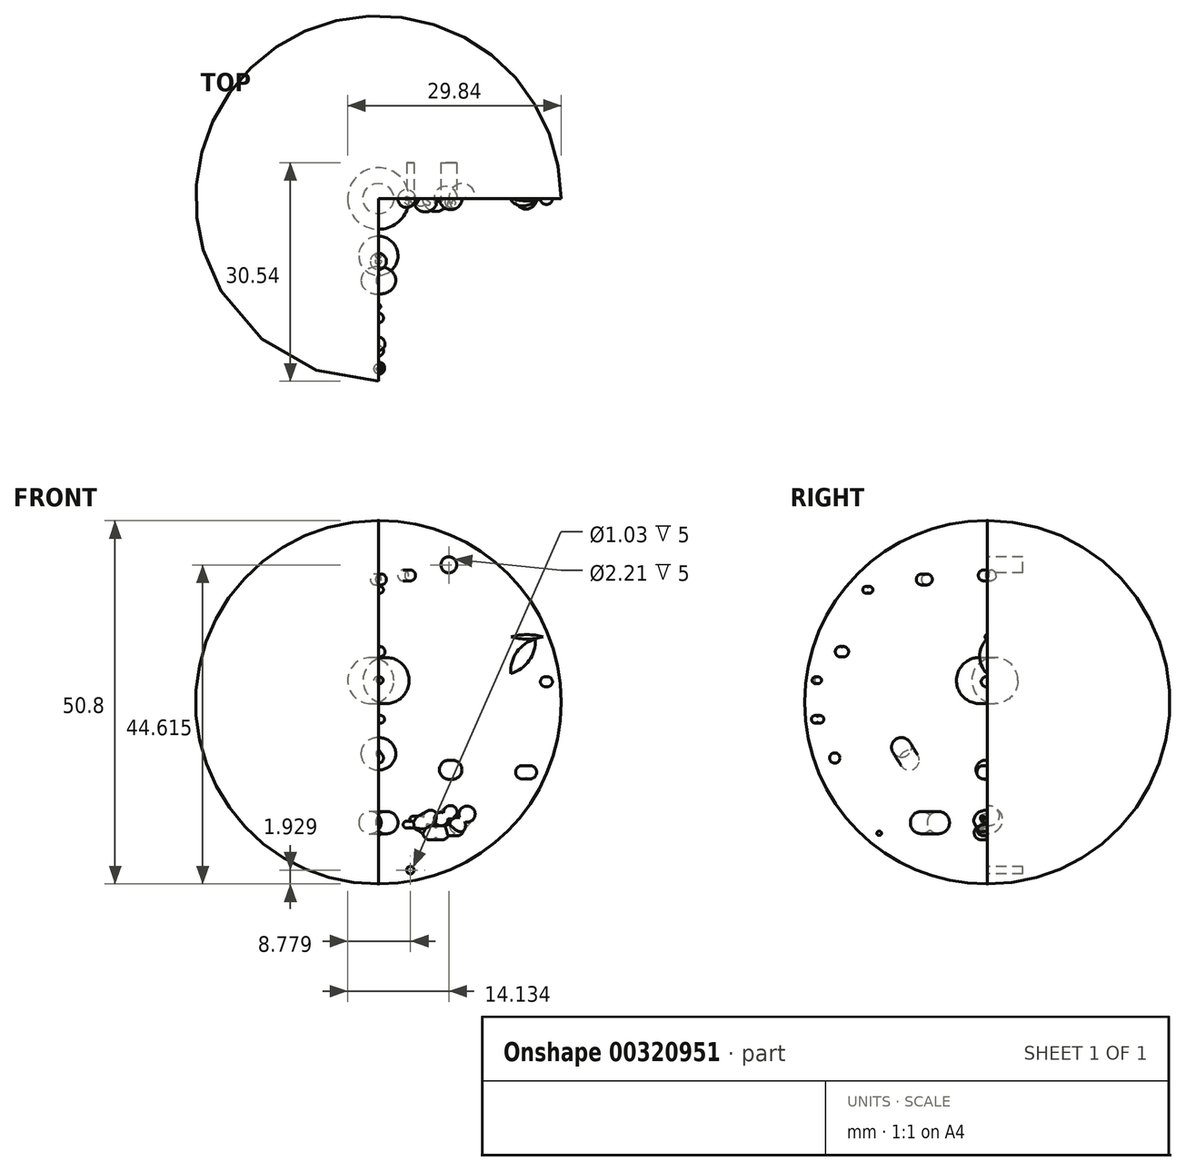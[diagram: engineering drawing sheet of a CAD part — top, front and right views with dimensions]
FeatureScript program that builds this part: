
annotation { "Feature Type Name" : "Feature", "Feature Type Description" : "" }
export const myFeature = defineFeature(function(context is Context, id is Id, definition is map)
    precondition{}
    {
        {
            var Q0;
            Q0=qCreatedBy(makeId("Front.planeOp"),FACE);
            var sketch = newSketch(context, id + "F0", { "sketchPlane" : qUnion([Q0])});
            skLineSegment(sketch, "E0", {"start": v(0, 0) * mm, "end": v(0, 50.8) * mm});
            skArc(sketch, "E1", {"start": v(0, 0) * mm, "mid": v(25.54, 25.4) * mm, "end": v(0, 50.8) * mm});
            skSolve(sketch);
        }
        {
            var Q0;
            Q0=makeQuery(id+"F0.imprint","IMPRINT",FACE,{"disambiguationData":[TD([[makeQuery(id+"F0.imprint","IMPRINT",EDGE,{"derivedFrom":sQuery(id+"F0.wireOp",EDGE,"E0")}),-1.0]])]});
            var Q1;
            Q1=sQuery(id+"F0.wireOp",EDGE,"E0");
            revolve(context, id + "F1", {"entities" : qUnion([Q0]), "axis" : qUnion([Q1]), "revolveType" : RevolveType.ONE_DIRECTION, "angle" : 270 * degree});
        }
        {
            var Q0;
            Q0=makeQuery(id+"F1.opRevolve","CAP_FACE",FACE,{"disambiguationData":[OSD([sQuery(id+"F0.wireOp",EDGE,"E0"),sQuery(id+"F0.wireOp",EDGE,"E1")])],"isStart":false});
            var sketch = newSketch(context, id + "F2", { "sketchPlane" : qUnion([Q0])});
            skLineSegment(sketch, "E2", {"start": v(0, 25.4) * mm, "end": v(0, 31.48) * mm});
            skArc(sketch, "E3", {"start": v(0, 31.48) * mm, "mid": v(-4.3, 28.44) * mm, "end": v(0, 25.4) * mm});
            skSolve(sketch);
        }
        {
            var Q0;
            Q0=makeQuery(id+"F2.imprint","IMPRINT",FACE,{"disambiguationData":[TD([[makeQuery(id+"F2.imprint","IMPRINT",EDGE,{"derivedFrom":sQuery(id+"F2.wireOp",EDGE,"E2")}),1.0]])]});
            var Q1;
            Q1=sQuery(id+"F2.wireOp",EDGE,"E2");
            revolve(context, id + "F3", {"entities" : qUnion([Q0]), "axis" : qUnion([Q1]), "revolveType" : RevolveType.FULL});
        }
        {
            var Q0;
            Q0=makeQuery(id+"F0.imprint","IMPRINT",FACE,{"disambiguationData":[TD([[makeQuery(id+"F0.imprint","IMPRINT",EDGE,{"derivedFrom":sQuery(id+"F0.wireOp",EDGE,"E0")}),-1.0]])]});
            var sketch = newSketch(context, id + "F4", { "sketchPlane" : qUnion([Q0])});
            skLineSegment(sketch, "E4", {"start": v(14.97, 35.22) * mm, "end": v(14.97, 32.76) * mm});
            skArc(sketch, "E5", {"start": v(14.97, 35.22) * mm, "mid": v(13.5, 33.99) * mm, "end": v(14.97, 32.76) * mm});
            skSolve(sketch);
        }
        {
            var Q0;
            Q0=sQuery(id+"F4.wireOp",EDGE,"E5");
            var Q1;
            Q1=sQuery(id+"F4.wireOp",EDGE,"E4");
            revolve(context, id + "F5", {"bodyType" : ToolBodyType.SURFACE, "surfaceEntities" : qUnion([Q0]), "axis" : qUnion([Q1]), "revolveType" : RevolveType.FULL});
        }
        {
            var Q0;
            Q0=makeQuery(id+"F0.imprint","IMPRINT",FACE,{"disambiguationData":[TD([[makeQuery(id+"F0.imprint","IMPRINT",EDGE,{"derivedFrom":sQuery(id+"F0.wireOp",EDGE,"E0")}),-1.0]])]});
            var sketch = newSketch(context, id + "F6", { "sketchPlane" : qUnion([Q0])});
            skLineSegment(sketch, "E6", {"start": v(10.1, 14.64) * mm, "end": v(10.1, 17.28) * mm});
            skArc(sketch, "E7", {"start": v(10.1, 14.64) * mm, "mid": v(11.67, 15.96) * mm, "end": v(10.1, 17.28) * mm});
            skSolve(sketch);
        }
        {
            var Q0;
            Q0=makeQuery(id+"F6.imprint","IMPRINT",FACE,{"disambiguationData":[TD([[makeQuery(id+"F6.imprint","IMPRINT",EDGE,{"derivedFrom":sQuery(id+"F6.wireOp",EDGE,"E6")}),-1.0]])]});
            var Q1;
            Q1=sQuery(id+"F6.wireOp",EDGE,"E6");
            revolve(context, id + "F7", {"operationType" : NewBodyOperationType.ADD, "entities" : qUnion([Q0]), "axis" : qUnion([Q1]), "revolveType" : RevolveType.FULL});
        }
        {
            var Q0;
            {var subQ0=sQuery(id+"F2.wireOp",EDGE,"E3");Q0=makeQuery(id+"F2.imprint","IMPRINT",FACE,{"disambiguationData":[TD([[makeQuery(id+"F2.imprint","IMPRINT",EDGE,{"derivedFrom":subQ0}),-1.0]])]});}
            var sketch = newSketch(context, id + "F8", { "sketchPlane" : qUnion([Q0])});
            skLineSegment(sketch, "E8", {"start": v(-21.3, 16.88) * mm, "end": v(-21.3, 18.33) * mm});
            skArc(sketch, "E9", {"start": v(-21.3, 16.88) * mm, "mid": v(-20.58, 17.6) * mm, "end": v(-21.3, 18.33) * mm});
            skSolve(sketch);
        }
        {
            var Q0;
            Q0=makeQuery(id+"F8.imprint","IMPRINT",FACE,{"disambiguationData":[TD([[makeQuery(id+"F8.imprint","IMPRINT",EDGE,{"derivedFrom":sQuery(id+"F8.wireOp",EDGE,"E8")}),-1.0]])]});
            var Q1;
            Q1=sQuery(id+"F8.wireOp",EDGE,"E8");
            revolve(context, id + "F9", {"operationType" : NewBodyOperationType.ADD, "entities" : qUnion([Q0]), "axis" : qUnion([Q1]), "revolveType" : RevolveType.FULL});
        }
        {
            var Q0;
            {var subQ0=sQuery(id+"F2.wireOp",EDGE,"E3");Q0=makeQuery(id+"F2.imprint","IMPRINT",FACE,{"disambiguationData":[TD([[makeQuery(id+"F2.imprint","IMPRINT",EDGE,{"derivedFrom":subQ0}),-1.0]])]});}
            var sketch = newSketch(context, id + "F10", { "sketchPlane" : qUnion([Q0])});
            skLineSegment(sketch, "E10", {"start": v(-16.7, 40.71) * mm, "end": v(-16.7, 41.53) * mm});
            skArc(sketch, "E11", {"start": v(-16.7, 40.71) * mm, "mid": v(-16, 41.12) * mm, "end": v(-16.7, 41.53) * mm});
            skSolve(sketch);
        }
        {
            var Q0;
            Q0 = qSketchRegion(id + "F10", true);
            var Q1;
            Q1=sQuery(id+"F10.wireOp",EDGE,"E10");
            revolve(context, id + "F11", {"operationType" : NewBodyOperationType.ADD, "entities" : qUnion([Q0]), "axis" : qUnion([Q1]), "revolveType" : RevolveType.FULL});
        }
        {
            var Q0;
            {var subQ0=sQuery(id+"F2.wireOp",EDGE,"E3");Q0=makeQuery(id+"F2.imprint","IMPRINT",FACE,{"disambiguationData":[TD([[makeQuery(id+"F2.imprint","IMPRINT",EDGE,{"derivedFrom":subQ0}),-1.0]])]});}
            var sketch = newSketch(context, id + "F12", { "sketchPlane" : qUnion([Q0])});
            skLineSegment(sketch, "E12", {"start": v(-15.1, 6.78) * mm, "end": v(-15.1, 7.37) * mm});
            skArc(sketch, "E13", {"start": v(-15.1, 6.78) * mm, "mid": v(-14.78, 7.08) * mm, "end": v(-15.1, 7.37) * mm});
            skSolve(sketch);
        }
        {
            var Q0;
            Q0 = qSketchRegion(id + "F12", true);
            var Q1;
            Q1=sQuery(id+"F12.wireOp",EDGE,"E12");
            revolve(context, id + "F13", {"operationType" : NewBodyOperationType.ADD, "entities" : qUnion([Q0]), "axis" : qUnion([Q1]), "revolveType" : RevolveType.FULL});
        }
        {
            var Q0;
            {var subQ0=sQuery(id+"F2.wireOp",EDGE,"E3");Q0=makeQuery(id+"F2.imprint","IMPRINT",FACE,{"disambiguationData":[TD([[makeQuery(id+"F2.imprint","IMPRINT",EDGE,{"derivedFrom":subQ0}),-1.0]])]});}
            var sketch = newSketch(context, id + "F14", { "sketchPlane" : qUnion([Q0])});
            skLineSegment(sketch, "E14", {"start": v(-23.82, 28.05) * mm, "end": v(-23.82, 28.9) * mm});
            skArc(sketch, "E15", {"start": v(-23.82, 28.05) * mm, "mid": v(-23.16, 28.48) * mm, "end": v(-23.82, 28.9) * mm});
            skSolve(sketch);
        }
        {
            var Q0;
            Q0 = qSketchRegion(id + "F14", true);
            var Q1;
            Q1=sQuery(id+"F14.wireOp",EDGE,"E14");
            revolve(context, id + "F15", {"entities" : qUnion([Q0]), "axis" : qUnion([Q1]), "revolveType" : RevolveType.FULL});
        }
        {
            var Q0;
            {var subQ0=sQuery(id+"F2.wireOp",EDGE,"E3");Q0=makeQuery(id+"F2.imprint","IMPRINT",FACE,{"disambiguationData":[TD([[makeQuery(id+"F2.imprint","IMPRINT",EDGE,{"derivedFrom":subQ0}),-1.0]])]});}
            var sketch = newSketch(context, id + "F16", { "sketchPlane" : qUnion([Q0])});
            skLineSegment(sketch, "E16", {"start": v(-8.01, 7.55) * mm, "end": v(-8.01, 9.6) * mm});
            skArc(sketch, "E17", {"start": v(-8.01, 9.6) * mm, "mid": v(-10.75, 8.57) * mm, "end": v(-8.01, 7.55) * mm});
            skSolve(sketch);
        }
        {
            var Q0;
            Q0 = qSketchRegion(id + "F16", true);
            var Q1;
            Q1=sQuery(id+"F16.wireOp",EDGE,"E16");
            revolve(context, id + "F17", {"entities" : qUnion([Q0]), "axis" : qUnion([Q1]), "revolveType" : RevolveType.FULL});
        }
        {
            var Q0;
            {var subQ0=sQuery(id+"F2.wireOp",EDGE,"E3");Q0=makeQuery(id+"F2.imprint","IMPRINT",FACE,{"disambiguationData":[TD([[makeQuery(id+"F2.imprint","IMPRINT",EDGE,{"derivedFrom":subQ0}),-1.0]])]});}
            var sketch = newSketch(context, id + "F18", { "sketchPlane" : qUnion([Q0])});
            skLineSegment(sketch, "E18", {"start": v(-12.2, 17.73) * mm, "end": v(-10.68, 18.67) * mm});
            skArc(sketch, "E19", {"start": v(-10.68, 18.67) * mm, "mid": v(-12.72, 20.27) * mm, "end": v(-12.2, 17.73) * mm});
            skSolve(sketch);
        }
        {
            var Q0;
            Q0=makeQuery(id+"F18.imprint","IMPRINT",FACE,{"disambiguationData":[TD([[makeQuery(id+"F18.imprint","IMPRINT",EDGE,{"derivedFrom":sQuery(id+"F18.wireOp",EDGE,"E18")}),1.0]])]});
            var Q1;
            Q1=sQuery(id+"F18.wireOp",EDGE,"E18");
            revolve(context, id + "F19", {"entities" : qUnion([Q0]), "axis" : qUnion([Q1]), "revolveType" : RevolveType.FULL});
        }
        {
            var Q0;
            {var subQ0=sQuery(id+"F2.wireOp",EDGE,"E3");Q0=makeQuery(id+"F2.imprint","IMPRINT",FACE,{"disambiguationData":[TD([[makeQuery(id+"F2.imprint","IMPRINT",EDGE,{"derivedFrom":subQ0}),-1.0]])]});}
            var sketch = newSketch(context, id + "F20", { "sketchPlane" : qUnion([Q0])});
            skLineSegment(sketch, "E20", {"start": v(-8.8, 41.91) * mm, "end": v(-8.8, 43.25) * mm});
            skArc(sketch, "E21", {"start": v(-8.8, 43.25) * mm, "mid": v(-9.92, 42.58) * mm, "end": v(-8.8, 41.91) * mm});
            skSolve(sketch);
        }
        {
            var Q0;
            Q0 = qSketchRegion(id + "F20", true);
            var Q1;
            Q1=sQuery(id+"F20.wireOp",EDGE,"E20");
            revolve(context, id + "F21", {"entities" : qUnion([Q0]), "axis" : qUnion([Q1]), "revolveType" : RevolveType.FULL});
        }
        {
            var Q0;
            Q0=makeQuery(id+"F4.imprint","IMPRINT",FACE,{"disambiguationData":[TD([[makeQuery(id+"F4.imprint","IMPRINT",EDGE,{"derivedFrom":sQuery(id+"F4.wireOp",EDGE,"E4")}),1.0]])]});
            var sketch = newSketch(context, id + "F22", { "sketchPlane" : qUnion([Q0])});
            skLineSegment(sketch, "E22", {"start": v(3.95, 42.57) * mm, "end": v(3.95, 43.72) * mm});
            skArc(sketch, "E23", {"start": v(3.95, 42.57) * mm, "mid": v(5.2, 43.14) * mm, "end": v(3.95, 43.72) * mm});
            skSolve(sketch);
        }
        {
            var Q0;
            Q0 = qSketchRegion(id + "F22", true);
            var Q1;
            Q1=sQuery(id+"F22.wireOp",EDGE,"E22");
            revolve(context, id + "F23", {"entities" : qUnion([Q0]), "axis" : qUnion([Q1]), "revolveType" : RevolveType.FULL});
        }
        {
            var Q0;
            Q0=makeQuery(id+"F0.imprint","IMPRINT",FACE,{"disambiguationData":[TD([[makeQuery(id+"F0.imprint","IMPRINT",EDGE,{"derivedFrom":sQuery(id+"F0.wireOp",EDGE,"E0")}),-1.0]])]});
            var sketch = newSketch(context, id + "F24", { "sketchPlane" : qUnion([Q0])});
            skCircle(sketch, "E24", {"center": v(4.48, 1.93) * mm, "radius": 0.52 * mm});
            skSolve(sketch);
        }
        {
            var Q0;
            Q0 = qSketchRegion(id + "F24", true);
            extrude(context, id + "F25", {"entities" : qUnion([Q0]), "operationType" : NewBodyOperationType.REMOVE, "oppositeDirection" : true, "depth" : 5 * mm});
        }
        {
            var Q0;
            Q0=makeQuery(id+"F0.imprint","IMPRINT",FACE,{"disambiguationData":[TD([[makeQuery(id+"F0.imprint","IMPRINT",EDGE,{"derivedFrom":sQuery(id+"F0.wireOp",EDGE,"E0")}),-1.0]])]});
            var sketch = newSketch(context, id + "F26", { "sketchPlane" : qUnion([Q0])});
            skCircle(sketch, "E25", {"center": v(9.83, 44.62) * mm, "radius": 1.1 * mm});
            skSolve(sketch);
        }
        {
            var Q0;
            Q0 = qSketchRegion(id + "F26", true);
            extrude(context, id + "F27", {"entities" : qUnion([Q0]), "operationType" : NewBodyOperationType.REMOVE, "oppositeDirection" : true, "depth" : 5 * mm});
        }
        {
            var Q0;
            Q0=makeQuery(id+"F6.imprint","IMPRINT",FACE,{"disambiguationData":[TD([[makeQuery(id+"F6.imprint","IMPRINT",EDGE,{"derivedFrom":sQuery(id+"F6.wireOp",EDGE,"E6")}),1.0]])]});
            var sketch = newSketch(context, id + "F28", { "sketchPlane" : qUnion([Q0])});
            skLineSegment(sketch, "E26", {"start": v(4.4, 8.04) * mm, "end": v(4.4, 8.54) * mm});
            skArc(sketch, "E27", {"start": v(4.4, 8.04) * mm, "mid": v(5.33, 8.3) * mm, "end": v(4.4, 8.54) * mm});
            skSolve(sketch);
        }
        {
            var Q0;
            Q0 = qSketchRegion(id + "F28", true);
            var Q1;
            Q1=sQuery(id+"F28.wireOp",EDGE,"E26");
            revolve(context, id + "F29", {"operationType" : NewBodyOperationType.ADD, "entities" : qUnion([Q0]), "axis" : qUnion([Q1]), "revolveType" : RevolveType.FULL});
        }
        {
            var Q0;
            Q0=makeQuery(id+"F0.imprint","IMPRINT",FACE,{"disambiguationData":[TD([[makeQuery(id+"F0.imprint","IMPRINT",EDGE,{"derivedFrom":sQuery(id+"F0.wireOp",EDGE,"E0")}),-1.0]])]});
            var sketch = newSketch(context, id + "F30", { "sketchPlane" : qUnion([Q0])});
            skLineSegment(sketch, "E28", {"start": v(5.2, 8.64) * mm, "end": v(5.2, 9.33) * mm});
            skArc(sketch, "E29", {"start": v(5.2, 8.64) * mm, "mid": v(6.02, 8.99) * mm, "end": v(5.2, 9.33) * mm});
            skSolve(sketch);
        }
        {
            var Q0;
            Q0 = qSketchRegion(id + "F30", true);
            var Q1;
            Q1=sQuery(id+"F30.wireOp",EDGE,"E28");
            revolve(context, id + "F31", {"operationType" : NewBodyOperationType.ADD, "entities" : qUnion([Q0]), "axis" : qUnion([Q1]), "revolveType" : RevolveType.FULL});
        }
        {
            var Q0;
            Q0=makeQuery(id+"F4.imprint","IMPRINT",FACE,{"disambiguationData":[TD([[makeQuery(id+"F4.imprint","IMPRINT",EDGE,{"derivedFrom":sQuery(id+"F4.wireOp",EDGE,"E4")}),1.0]])]});
            var sketch = newSketch(context, id + "F32", { "sketchPlane" : qUnion([Q0])});
            skLineSegment(sketch, "E30", {"start": v(5.97, 8.18) * mm, "end": v(5.72, 7.87) * mm});
            skArc(sketch, "E31", {"start": v(5.72, 7.87) * mm, "mid": v(6.76, 7.3) * mm, "end": v(5.97, 8.18) * mm});
            skSolve(sketch);
        }
        {
            var Q0;
            Q0=makeQuery(id+"F32.imprint","IMPRINT",FACE,{"disambiguationData":[TD([[makeQuery(id+"F32.imprint","IMPRINT",EDGE,{"derivedFrom":sQuery(id+"F32.wireOp",EDGE,"E30")}),1.0]])]});
            var Q1;
            Q1=sQuery(id+"F32.wireOp",EDGE,"E30");
            revolve(context, id + "F33", {"operationType" : NewBodyOperationType.ADD, "entities" : qUnion([Q0]), "axis" : qUnion([Q1]), "revolveType" : RevolveType.FULL});
        }
        {
            var Q0;
            Q0=makeQuery(id+"F0.imprint","IMPRINT",FACE,{"disambiguationData":[TD([[makeQuery(id+"F0.imprint","IMPRINT",EDGE,{"derivedFrom":sQuery(id+"F0.wireOp",EDGE,"E0")}),-1.0]])]});
            var sketch = newSketch(context, id + "F34", { "sketchPlane" : qUnion([Q0])});
            skLineSegment(sketch, "E32", {"start": v(6.8, 8.44) * mm, "end": v(6.3, 9.3) * mm});
            skArc(sketch, "E33", {"start": v(6.8, 8.44) * mm, "mid": v(8.17, 9.8) * mm, "end": v(6.3, 9.3) * mm});
            skSolve(sketch);
        }
        {
            var Q0;
            Q0=makeQuery(id+"F34.imprint","IMPRINT",FACE,{"disambiguationData":[TD([[makeQuery(id+"F34.imprint","IMPRINT",EDGE,{"derivedFrom":sQuery(id+"F34.wireOp",EDGE,"E32")}),-1.0]])]});
            var Q1;
            Q1=sQuery(id+"F34.wireOp",EDGE,"E32");
            revolve(context, id + "F35", {"operationType" : NewBodyOperationType.ADD, "entities" : qUnion([Q0]), "axis" : qUnion([Q1]), "revolveType" : RevolveType.FULL});
        }
        {
            var Q0;
            Q0=makeQuery(id+"F0.imprint","IMPRINT",FACE,{"disambiguationData":[TD([[makeQuery(id+"F0.imprint","IMPRINT",EDGE,{"derivedFrom":sQuery(id+"F0.wireOp",EDGE,"E0")}),-1.0]])]});
            var sketch = newSketch(context, id + "F36", { "sketchPlane" : qUnion([Q0])});
            skLineSegment(sketch, "E34", {"start": v(8.03, 7.75) * mm, "end": v(8.03, 6.56) * mm});
            skArc(sketch, "E35", {"start": v(8.03, 6.56) * mm, "mid": v(9.85, 7.15) * mm, "end": v(8.03, 7.75) * mm});
            skSolve(sketch);
        }
        {
            var Q0;
            Q0 = qSketchRegion(id + "F36", true);
            var Q1;
            Q1=sQuery(id+"F36.wireOp",EDGE,"E34");
            revolve(context, id + "F37", {"operationType" : NewBodyOperationType.ADD, "entities" : qUnion([Q0]), "axis" : qUnion([Q1]), "revolveType" : RevolveType.FULL});
        }
        {
            var Q0;
            Q0=makeQuery(id+"F4.imprint","IMPRINT",FACE,{"disambiguationData":[TD([[makeQuery(id+"F4.imprint","IMPRINT",EDGE,{"derivedFrom":sQuery(id+"F4.wireOp",EDGE,"E4")}),1.0]])]});
            var sketch = newSketch(context, id + "F38", { "sketchPlane" : qUnion([Q0])});
            skLineSegment(sketch, "E36", {"start": v(9.71, 9.14) * mm, "end": v(9.12, 9.94) * mm});
            skArc(sketch, "E37", {"start": v(9.71, 9.14) * mm, "mid": v(10.83, 10.57) * mm, "end": v(9.12, 9.94) * mm});
            skSolve(sketch);
        }
        {
            var Q0;
            Q0 = qSketchRegion(id + "F38", true);
            var Q1;
            Q1=sQuery(id+"F38.wireOp",EDGE,"E36");
            revolve(context, id + "F39", {"operationType" : NewBodyOperationType.ADD, "entities" : qUnion([Q0]), "axis" : qUnion([Q1]), "revolveType" : RevolveType.FULL});
        }
        {
            var Q0;
            Q0=makeQuery(id+"F0.imprint","IMPRINT",FACE,{"disambiguationData":[TD([[makeQuery(id+"F0.imprint","IMPRINT",EDGE,{"derivedFrom":sQuery(id+"F0.wireOp",EDGE,"E0")}),-1.0]])]});
            var sketch = newSketch(context, id + "F40", { "sketchPlane" : qUnion([Q0])});
            skLineSegment(sketch, "E38", {"start": v(10.5, 7) * mm, "end": v(10.5, 8.04) * mm});
            skArc(sketch, "E39", {"start": v(10.5, 7) * mm, "mid": v(11.87, 7.52) * mm, "end": v(10.5, 8.04) * mm});
            skSolve(sketch);
        }
        {
            var Q0;
            Q0 = qSketchRegion(id + "F40", true);
            var Q1;
            Q1=sQuery(id+"F40.wireOp",EDGE,"E38");
            revolve(context, id + "F41", {"operationType" : NewBodyOperationType.ADD, "entities" : qUnion([Q0]), "axis" : qUnion([Q1]), "revolveType" : RevolveType.FULL});
        }
        {
            var Q0;
            Q0=makeQuery(id+"F4.imprint","IMPRINT",FACE,{"disambiguationData":[TD([[makeQuery(id+"F4.imprint","IMPRINT",EDGE,{"derivedFrom":sQuery(id+"F4.wireOp",EDGE,"E4")}),1.0]])]});
            var sketch = newSketch(context, id + "F42", { "sketchPlane" : qUnion([Q0])});
            skLineSegment(sketch, "E40", {"start": v(12.06, 8.69) * mm, "end": v(11.39, 9.26) * mm});
            skArc(sketch, "E41", {"start": v(12.06, 8.69) * mm, "mid": v(13.12, 10.62) * mm, "end": v(11.39, 9.26) * mm});
            skSolve(sketch);
        }
        {
            var Q0;
            Q0 = qSketchRegion(id + "F42", true);
            var Q1;
            Q1=sQuery(id+"F42.wireOp",EDGE,"E40");
            revolve(context, id + "F43", {"operationType" : NewBodyOperationType.ADD, "entities" : qUnion([Q0]), "axis" : qUnion([Q1]), "revolveType" : RevolveType.FULL});
        }
        {
            var Q0;
            Q0=makeQuery(id+"F4.imprint","IMPRINT",FACE,{"disambiguationData":[TD([[makeQuery(id+"F4.imprint","IMPRINT",EDGE,{"derivedFrom":sQuery(id+"F4.wireOp",EDGE,"E4")}),1.0]])]});
            var sketch = newSketch(context, id + "F44", { "sketchPlane" : qUnion([Q0])});
            skFitSpline(sketch, "E42", {"points": [v(8.62, 26.93) * mm, v(6.94, 22.5) * mm, v(9.64, 30.44) * mm, v(8.56, 23.37) * mm, v(10.96, 30.88) * mm, v(9.88, 22.13) * mm, v(12.08, 30.38) * mm, v(11.49, 23.3) * mm, v(13.38, 29.03) * mm, v(13.48, 22.05) * mm, v(15.33, 30.87) * mm, v(14.55, 22.1) * mm, v(16.73, 29.86) * mm, v(17.13, 22.24) * mm], "startDerivative": vector(-46.02, -129.46) * mm, "endDerivative": vector(-4.13, -170.12) * mm});
            skSolve(sketch);
        }
        {
            var Q0;
            Q0=sQuery(id+"F44.wireOp",EDGE,"E42");
            extrude(context, id + "F45", {"bodyType" : ToolBodyType.SURFACE, "surfaceEntities" : qUnion([Q0]), "depth" : 3 * mm});
        }
        {
            var Q0;
            {var subQ0=sQuery(id+"F2.wireOp",EDGE,"E3");Q0=makeQuery(id+"F2.imprint","IMPRINT",FACE,{"disambiguationData":[TD([[makeQuery(id+"F2.imprint","IMPRINT",EDGE,{"derivedFrom":subQ0}),-1.0]])]});}
            var sketch = newSketch(context, id + "F46", { "sketchPlane" : qUnion([Q0])});
            skLineSegment(sketch, "E43", {"start": v(-20.3, 31.78) * mm, "end": v(-20.3, 33.16) * mm});
            skArc(sketch, "E44", {"start": v(-20.3, 31.78) * mm, "mid": v(-19.37, 32.47) * mm, "end": v(-20.3, 33.16) * mm});
            skSolve(sketch);
        }
        {
            var Q0;
            Q0 = qSketchRegion(id + "F46", true);
            var Q1;
            Q1=sQuery(id+"F46.wireOp",EDGE,"E43");
            revolve(context, id + "F47", {"operationType" : NewBodyOperationType.ADD, "entities" : qUnion([Q0]), "axis" : qUnion([Q1]), "revolveType" : RevolveType.FULL});
        }
        {
            var Q0;
            {var subQ0=sQuery(id+"F2.wireOp",EDGE,"E3");Q0=makeQuery(id+"F2.imprint","IMPRINT",FACE,{"disambiguationData":[TD([[makeQuery(id+"F2.imprint","IMPRINT",EDGE,{"derivedFrom":subQ0}),-1.0]])]});}
            var sketch = newSketch(context, id + "F48", { "sketchPlane" : qUnion([Q0])});
            skLineSegment(sketch, "E45", {"start": v(-23.71, 22.6) * mm, "end": v(-23.71, 23.43) * mm});
            skArc(sketch, "E46", {"start": v(-23.71, 23.43) * mm, "mid": v(-24.58, 23.01) * mm, "end": v(-23.71, 22.6) * mm});
            skSolve(sketch);
        }
        {
            var Q0;
            Q0=makeQuery(id+"F48.imprint","IMPRINT",FACE,{"disambiguationData":[TD([[makeQuery(id+"F48.imprint","IMPRINT",EDGE,{"derivedFrom":sQuery(id+"F48.wireOp",EDGE,"E45")}),1.0]])]});
            var Q1;
            Q1=sQuery(id+"F48.wireOp",EDGE,"E45");
            revolve(context, id + "F49", {"operationType" : NewBodyOperationType.ADD, "entities" : qUnion([Q0]), "axis" : qUnion([Q1]), "revolveType" : RevolveType.FULL});
        }
        {
            var Q0;
            Q0=makeQuery(id+"F6.imprint","IMPRINT",FACE,{"disambiguationData":[TD([[makeQuery(id+"F6.imprint","IMPRINT",EDGE,{"derivedFrom":sQuery(id+"F6.wireOp",EDGE,"E6")}),1.0]])]});
            var sketch = newSketch(context, id + "F50", { "sketchPlane" : qUnion([Q0])});
            skLineSegment(sketch, "E47", {"start": v(20.64, 14.86) * mm, "end": v(20.64, 16.36) * mm});
            skArc(sketch, "E48", {"start": v(20.64, 14.86) * mm, "mid": v(22.11, 15.6) * mm, "end": v(20.64, 16.36) * mm});
            skSolve(sketch);
        }
        {
            var Q0;
            Q0 = qSketchRegion(id + "F50", true);
            var Q1;
            Q1=sQuery(id+"F50.wireOp",EDGE,"E47");
            revolve(context, id + "F51", {"operationType" : NewBodyOperationType.ADD, "entities" : qUnion([Q0]), "axis" : qUnion([Q1]), "revolveType" : RevolveType.FULL});
        }
        {
            var Q0;
            Q0=makeQuery(id+"F4.imprint","IMPRINT",FACE,{"disambiguationData":[TD([[makeQuery(id+"F4.imprint","IMPRINT",EDGE,{"derivedFrom":sQuery(id+"F4.wireOp",EDGE,"E4")}),1.0]])]});
            var sketch = newSketch(context, id + "F52", { "sketchPlane" : qUnion([Q0])});
            skLineSegment(sketch, "E49", {"start": v(23.48, 27.59) * mm, "end": v(23.48, 28.96) * mm});
            skArc(sketch, "E50", {"start": v(23.48, 27.59) * mm, "mid": v(24.33, 28.27) * mm, "end": v(23.48, 28.96) * mm});
            skSolve(sketch);
        }
        {
            var Q0;
            Q0 = qSketchRegion(id + "F52", true);
            var Q1;
            Q1=sQuery(id+"F52.wireOp",EDGE,"E49");
            revolve(context, id + "F53", {"operationType" : NewBodyOperationType.ADD, "entities" : qUnion([Q0]), "axis" : qUnion([Q1]), "revolveType" : RevolveType.FULL});
        }
        {
            var Q0;
            Q0=makeQuery(id+"F0.imprint","IMPRINT",FACE,{"disambiguationData":[TD([[makeQuery(id+"F0.imprint","IMPRINT",EDGE,{"derivedFrom":sQuery(id+"F0.wireOp",EDGE,"E0")}),-1.0]])]});
            var sketch = newSketch(context, id + "F54", { "sketchPlane" : qUnion([Q0])});
            skLineSegment(sketch, "E51", {"start": v(18.5, 29.43) * mm, "end": v(21.92, 34.23) * mm});
            skArc(sketch, "E52", {"start": v(18.5, 29.43) * mm, "mid": v(21.07, 31.23) * mm, "end": v(21.92, 34.23) * mm});
            skSolve(sketch);
        }
        {
            var Q0;
            Q0 = qSketchRegion(id + "F54", true);
            var Q1;
            Q1=sQuery(id+"F54.wireOp",EDGE,"E51");
            revolve(context, id + "F55", {"operationType" : NewBodyOperationType.ADD, "entities" : qUnion([Q0]), "axis" : qUnion([Q1]), "revolveType" : RevolveType.FULL});
        }
        {
            var Q0;
            Q0=makeQuery(id+"F6.imprint","IMPRINT",FACE,{"disambiguationData":[TD([[makeQuery(id+"F6.imprint","IMPRINT",EDGE,{"derivedFrom":sQuery(id+"F6.wireOp",EDGE,"E6")}),1.0]])]});
            var sketch = newSketch(context, id + "F56", { "sketchPlane" : qUnion([Q0])});
            skLineSegment(sketch, "E53", {"start": v(18.56, 34.55) * mm, "end": v(23, 34.55) * mm});
            skArc(sketch, "E54", {"start": v(23, 34.55) * mm, "mid": v(20.78, 34.86) * mm, "end": v(18.56, 34.55) * mm});
            skSolve(sketch);
        }
        {
            var Q0;
            Q0 = qSketchRegion(id + "F56", true);
            var Q1;
            Q1=sQuery(id+"F56.wireOp",EDGE,"E53");
            revolve(context, id + "F57", {"operationType" : NewBodyOperationType.ADD, "entities" : qUnion([Q0]), "axis" : qUnion([Q1]), "revolveType" : RevolveType.FULL});
        }
    });
